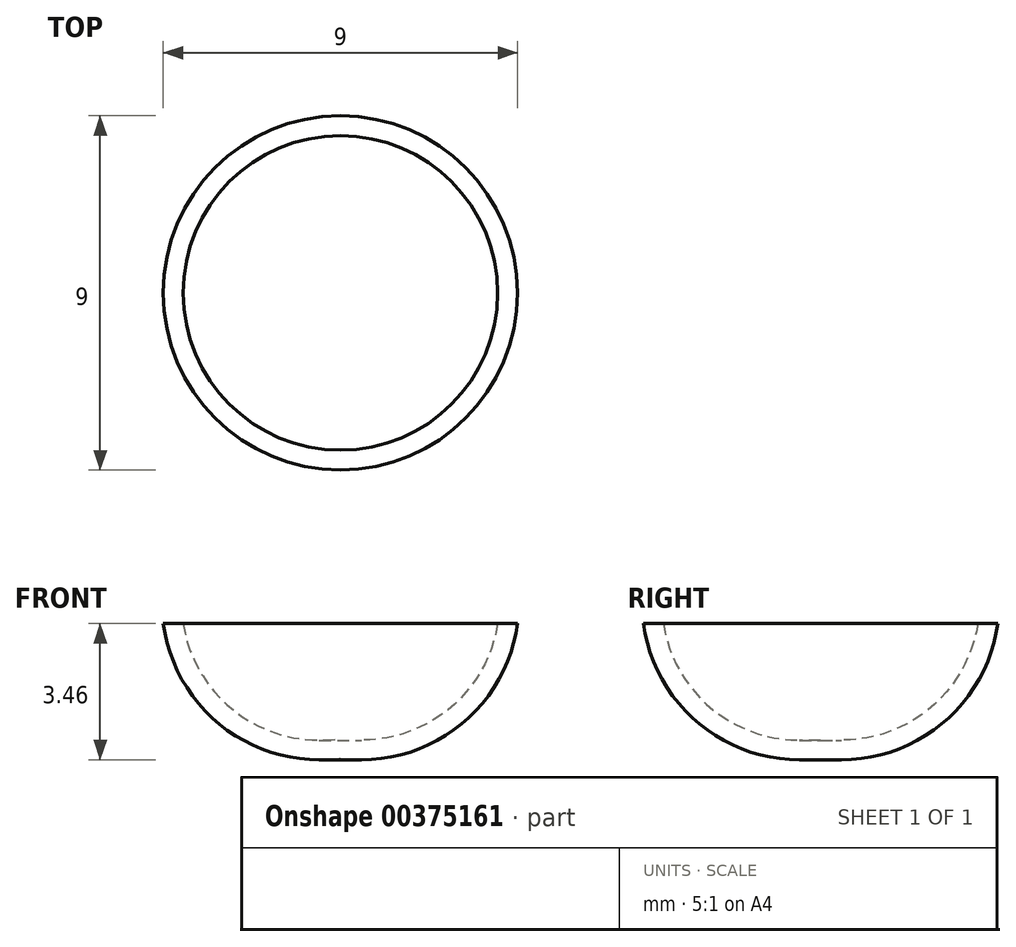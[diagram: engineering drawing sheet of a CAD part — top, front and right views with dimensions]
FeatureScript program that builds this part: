
annotation { "Feature Type Name" : "Feature", "Feature Type Description" : "" }
export const myFeature = defineFeature(function(context is Context, id is Id, definition is map)
    precondition{}
    {
        {
            var Q0;
            Q0=qCreatedBy(makeId("Front.planeOp"),FACE);
            var sketch = newSketch(context, id + "F0", { "sketchPlane" : qUnion([Q0])});
            skLineSegment(sketch, "E0", {"start": v(0, 15.83) * mm, "end": v(0, -9.43) * mm, "construction": true});
            skLineSegment(sketch, "E1", {"start": v(0, 0) * mm, "end": v(4.5, 0) * mm});
            skLineSegment(sketch, "E2", {"start": v(0, 0) * mm, "end": v(0, 4.5) * mm});
            skArc(sketch, "E3", {"start": v(4.5, 0) * mm, "mid": v(3.36, 3.36) * mm, "end": v(0, 4.5) * mm});
            skSolve(sketch);
        }
        {
            var Q0;
            Q0 = qSketchRegion(id + "F0", true);
            var Q1;
            Q1=sQuery(id+"F0.wireOp",EDGE,"E2");
            revolve(context, id + "F1", {"entities" : qUnion([Q0]), "axis" : qUnion([Q1]), "revolveType" : RevolveType.FULL});
        }
        {
            var Q0;
            Q0=makeQuery(id+"F1.opRevolve","SWEPT_FACE",FACE,{"disambiguationData":[OSD([sQuery(id+"F0.wireOp",EDGE,"E1")])]});
            shell(context, id + "F2", {"entities" : qUnion([Q0]), "thickness" : 0.5 * mm});
        }
    });
